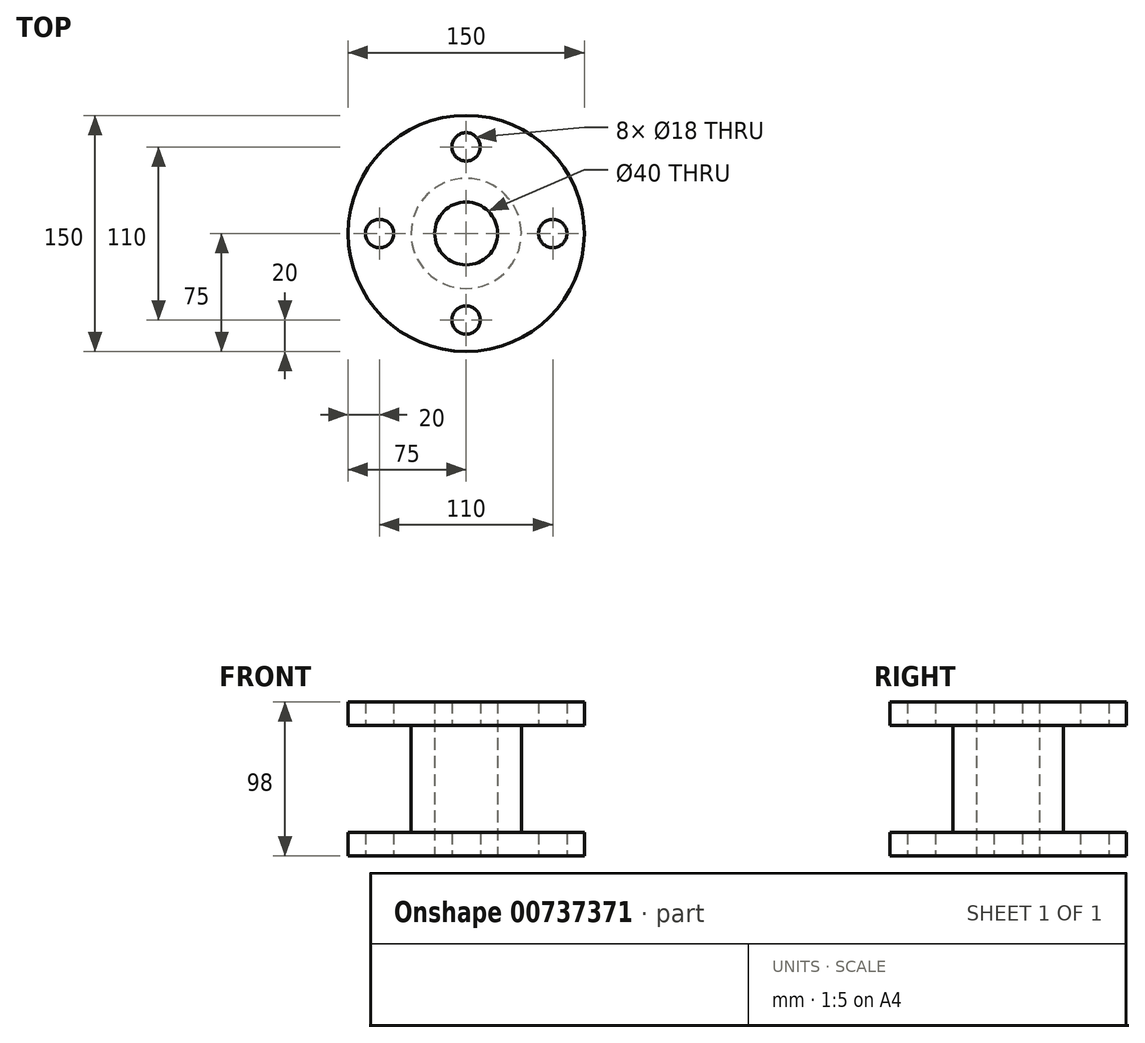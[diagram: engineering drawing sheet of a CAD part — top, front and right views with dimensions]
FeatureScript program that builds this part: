
annotation { "Feature Type Name" : "Feature", "Feature Type Description" : "" }
export const myFeature = defineFeature(function(context is Context, id is Id, definition is map)
    precondition{}
    {
        {
            var Q0;
            Q0=qCreatedBy(makeId("Top.planeOp"),FACE);
            var sketch = newSketch(context, id + "F0", { "sketchPlane" : qUnion([Q0])});
            skCircle(sketch, "E0", {"center": v(0, 0) * mm, "radius": 75 * mm});
            skCircle(sketch, "E1", {"center": v(0, 0) * mm, "radius": 20 * mm});
            skCircle(sketch, "E2", {"center": v(0, 55) * mm, "radius": 9 * mm});
            skCircle(sketch, "E3.1.0", {"center": v(-55, 0) * mm, "radius": 9 * mm});
            skCircle(sketch, "E3.2.0", {"center": v(0, -55) * mm, "radius": 9 * mm});
            skCircle(sketch, "E3.3.0", {"center": v(55, 0) * mm, "radius": 9 * mm});
            skSolve(sketch);
        }
        {
            var Q0;
            Q0=makeQuery(id+"F0.imprint","IMPRINT",FACE,{"disambiguationData":[TD([[makeQuery(id+"F0.imprint","IMPRINT",EDGE,{"derivedFrom":sQuery(id+"F0.wireOp",EDGE,"E0")}),1.0]])]});
            extrude(context, id + "F1", {"entities" : qUnion([Q0]), "depth" : 15 * mm, "offsetDistance" : 25 * mm});
        }
        {
            var Q0;
            Q0=makeQuery(id+"F1.opExtrude","CAP_FACE",FACE,{"disambiguationData":[OSD([sQuery(id+"F0.wireOp",EDGE,"E0"),sQuery(id+"F0.wireOp",EDGE,"E1"),sQuery(id+"F0.wireOp",EDGE,"E2"),sQuery(id+"F0.wireOp",EDGE,"E3.1.0"),sQuery(id+"F0.wireOp",EDGE,"E3.2.0"),sQuery(id+"F0.wireOp",EDGE,"E3.3.0")])],"isStart":false});
            var sketch = newSketch(context, id + "F2", { "sketchPlane" : qUnion([Q0])});
            skCircle(sketch, "E4", {"center": v(0, 0) * mm, "radius": 35 * mm});
            skSolve(sketch);
        }
        {
            var Q0;
            Q0=makeQuery(id+"F2.imprint","IMPRINT",FACE,{"disambiguationData":[TD([[makeQuery(id+"F2.imprint","IMPRINT",EDGE,{"derivedFrom":sQuery(id+"F2.wireOp",EDGE,"E4")}),1.0]])]});
            extrude(context, id + "F3", {"entities" : qUnion([Q0]), "operationType" : NewBodyOperationType.ADD, "depth" : 68 * mm, "offsetDistance" : 25 * mm});
        }
        {
            var Q0;
            Q0=makeQuery(id+"F3.opExtrude","CAP_FACE",FACE,{"disambiguationData":[OSD([sQuery(id+"F0.wireOp",EDGE,"E1"),sQuery(id+"F2.wireOp",EDGE,"E4")])],"isStart":false});
            var sketch = newSketch(context, id + "F4", { "sketchPlane" : qUnion([Q0])});
            skCircle(sketch, "E5.0", {"center": v(0, 0) * mm, "radius": 20 * mm});
            skCircle(sketch, "E6.0.0", {"center": v(0, 0) * mm, "radius": 75 * mm});
            skCircle(sketch, "E7.0", {"center": v(55, 0) * mm, "radius": 9 * mm});
            skCircle(sketch, "E8.0", {"center": v(-55, 0) * mm, "radius": 9 * mm});
            skCircle(sketch, "E9.0", {"center": v(0, 55) * mm, "radius": 9 * mm});
            skCircle(sketch, "E10.0", {"center": v(0, -55) * mm, "radius": 9 * mm});
            skSolve(sketch);
        }
        {
            var Q0;
            Q0 = qSketchRegion(id + "F4", true);
            extrude(context, id + "F5", {"entities" : qUnion([Q0]), "operationType" : NewBodyOperationType.ADD, "depth" : 15 * mm, "offsetDistance" : 25 * mm});
        }
    });
